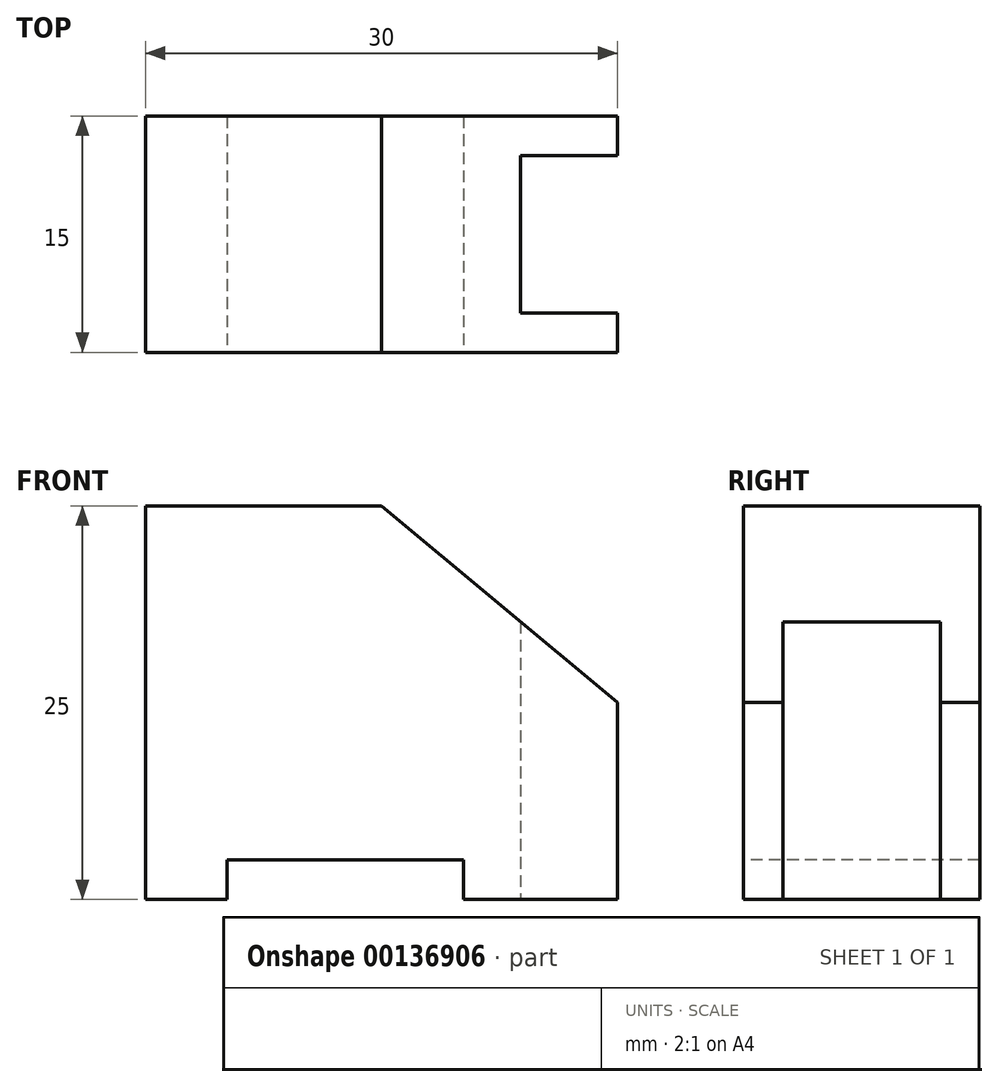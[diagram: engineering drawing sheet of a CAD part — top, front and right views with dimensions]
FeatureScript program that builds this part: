
annotation { "Feature Type Name" : "Feature", "Feature Type Description" : "" }
export const myFeature = defineFeature(function(context is Context, id is Id, definition is map)
    precondition{}
    {
        {
            var Q0;
            Q0=qCreatedBy(makeId("Top.planeOp"),FACE);
            var sketch = newSketch(context, id + "F0", { "sketchPlane" : qUnion([Q0])});
            skLineSegment(sketch, "E0", {"start": v(0, 0) * mm, "end": v(0, 15) * mm});
            skLineSegment(sketch, "E1", {"start": v(0, 15) * mm, "end": v(30, 15) * mm});
            skLineSegment(sketch, "E2", {"start": v(30, 15) * mm, "end": v(30, 12.5) * mm});
            skLineSegment(sketch, "E3", {"start": v(30, 12.5) * mm, "end": v(23.84, 12.5) * mm});
            skLineSegment(sketch, "E4", {"start": v(23.84, 12.5) * mm, "end": v(23.84, 2.5) * mm});
            skLineSegment(sketch, "E5", {"start": v(23.84, 2.5) * mm, "end": v(30, 2.5) * mm});
            skLineSegment(sketch, "E6", {"start": v(30, 2.5) * mm, "end": v(30, 0) * mm});
            skLineSegment(sketch, "E7", {"start": v(30, 0) * mm, "end": v(0, 0) * mm});
            skSolve(sketch);
        }
        {
            var Q0;
            Q0 = qSketchRegion(id + "F0", true);
            extrude(context, id + "F1", {"entities" : qUnion([Q0]), "depth" : 25 * mm});
        }
        {
            var Q0;
            Q0=makeQuery(id+"F1.opExtrude","SWEPT_FACE",FACE,{"disambiguationData":[OSD([sQuery(id+"F0.wireOp",EDGE,"E7")])]});
            var sketch = newSketch(context, id + "F2", { "sketchPlane" : qUnion([Q0])});
            skLineSegment(sketch, "E8", {"start": v(15, 25) * mm, "end": v(30, 12.5) * mm});
            skLineSegment(sketch, "E9", {"start": v(30, 12.5) * mm, "end": v(30, 25) * mm});
            skLineSegment(sketch, "E10", {"start": v(30, 25) * mm, "end": v(15, 25) * mm});
            skSolve(sketch);
        }
        {
            var Q0;
            Q0=makeQuery(id+"F2.imprint","IMPRINT",FACE,{"disambiguationData":[TD([[makeQuery(id+"F2.imprint","IMPRINT",EDGE,{"derivedFrom":sQuery(id+"F2.wireOp",EDGE,"E8")}),1.0]])]});
            extrude(context, id + "F3", {"entities" : qUnion([Q0]), "operationType" : NewBodyOperationType.REMOVE, "oppositeDirection" : true, "depth" : 25 * mm});
        }
        {
            var Q0;
            Q0=makeQuery(id+"F1.opExtrude","SWEPT_FACE",FACE,{"disambiguationData":[OSD([sQuery(id+"F0.wireOp",EDGE,"E7")])]});
            var sketch = newSketch(context, id + "F4", { "sketchPlane" : qUnion([Q0])});
            skLineSegment(sketch, "E11", {"start": v(5.2, 0) * mm, "end": v(5.2, 2.5) * mm});
            skLineSegment(sketch, "E12", {"start": v(5.2, 2.5) * mm, "end": v(20.2, 2.5) * mm});
            skLineSegment(sketch, "E13", {"start": v(20.2, 2.5) * mm, "end": v(20.2, 0) * mm});
            skLineSegment(sketch, "E14", {"start": v(20.2, 0) * mm, "end": v(5.2, 0) * mm});
            skSolve(sketch);
        }
        {
            var Q0;
            Q0 = qSketchRegion(id + "F4", true);
            extrude(context, id + "F5", {"entities" : qUnion([Q0]), "operationType" : NewBodyOperationType.REMOVE, "oppositeDirection" : true, "depth" : 25 * mm});
        }
    });
